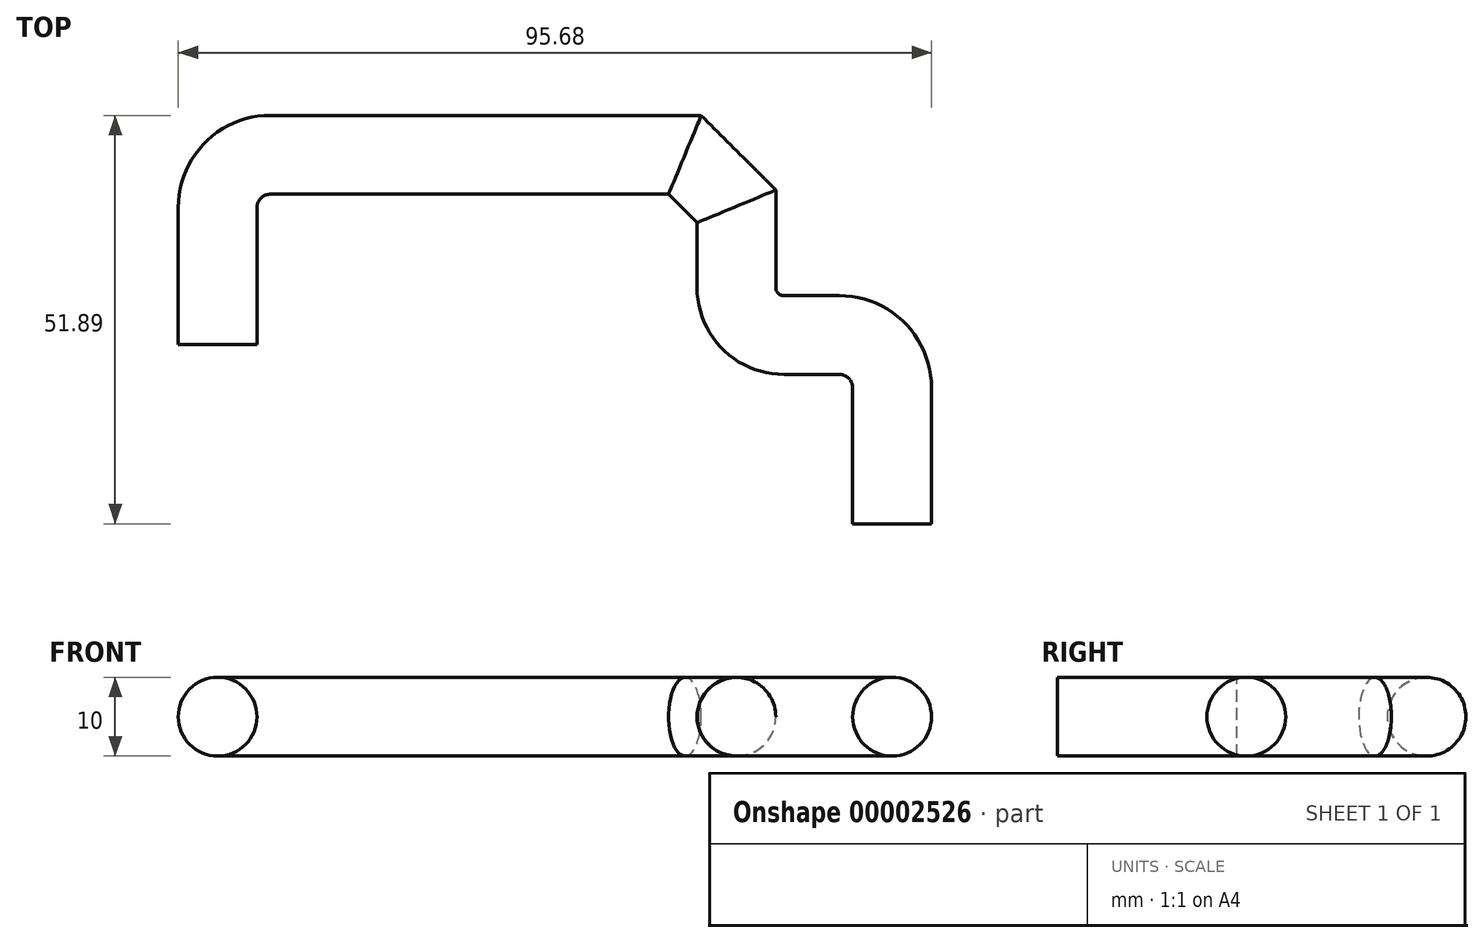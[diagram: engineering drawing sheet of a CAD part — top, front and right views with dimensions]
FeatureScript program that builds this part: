
annotation { "Feature Type Name" : "Feature", "Feature Type Description" : "" }
export const myFeature = defineFeature(function(context is Context, id is Id, definition is map)
    precondition{}
    {
        {
            var Q0;
            Q0=qCreatedBy(makeId("Top.planeOp"),FACE);
            var sketch = newSketch(context, id + "F0", { "sketchPlane" : qUnion([Q0])});
            skLineSegment(sketch, "E0", {"start": v(-28.39, -23.74) * mm, "end": v(-28.39, -6.35) * mm});
            skLineSegment(sketch, "E1", {"start": v(-22.04, 0) * mm, "end": v(30.49, 0) * mm});
            skLineSegment(sketch, "E2", {"start": v(36.84, -6.35) * mm, "end": v(36.84, -16.55) * mm});
            skLineSegment(sketch, "E3", {"start": v(43.19, -22.9) * mm, "end": v(50.26, -22.9) * mm});
            skLineSegment(sketch, "E4", {"start": v(56.6, -29.25) * mm, "end": v(56.6, -46.55) * mm});
            skPoint(sketch, "E5.visualSharp", {"position": v(-28.39, 0) * mm});
            skArc(sketch, "E5.filletArc", {"start": v(-22.04, 0) * mm, "mid": v(-26.53, -1.86) * mm, "end": v(-28.39, -6.35) * mm});
            skPoint(sketch, "E6.visualSharp", {"position": v(36.84, 0) * mm});
            skPoint(sketch, "E7.visualSharp", {"position": v(36.84, -22.9) * mm});
            skArc(sketch, "E7.filletArc", {"start": v(36.84, -16.55) * mm, "mid": v(38.7, -21.04) * mm, "end": v(43.19, -22.9) * mm});
            skPoint(sketch, "E8.visualSharp", {"position": v(56.6, -22.9) * mm});
            skArc(sketch, "E8.filletArc", {"start": v(56.6, -29.25) * mm, "mid": v(54.75, -24.76) * mm, "end": v(50.26, -22.9) * mm});
            skLineSegment(sketch, "E9", {"start": v(30.49, 0) * mm, "end": v(36.84, -6.35) * mm});
            skSolve(sketch);
        }
        {
            var Q0;
            Q0=qCreatedBy(makeId("Front.planeOp"),FACE);
            var Q1;
            Q1=sQuery(id+"F0.wireOp",VERTEX,"E0.start");
            cPlane(context, id + "F1", {"entities" : qUnion([Q0, Q1]), "cplaneType" : CPlaneType.PLANE_POINT, "offset" : 152.4 * mm, "width" : 152.4 * mm, "height" : 152.4 * mm});
        }
        {
            var Q0;
            Q0=qCreatedBy(id+"F1.planeOp",FACE);
            var sketch = newSketch(context, id + "F2", { "sketchPlane" : qUnion([Q0])});
            skCircle(sketch, "E10", {"center": v(-28.73, 0) * mm, "radius": 5 * mm});
            skSolve(sketch);
        }
        {
            var Q0;
            Q0 = qSketchRegion(id + "F2", true);
            var Q1;
            Q1=sQuery(id+"F0.wireOp",EDGE,"E0");
            var Q2;
            Q2=sQuery(id+"F0.wireOp",EDGE,"E5.filletArc");
            var Q3;
            Q3=sQuery(id+"F0.wireOp",EDGE,"E1");
            var Q4;
            Q4=sQuery(id+"F0.wireOp",EDGE,"E6.filletArc");
            var Q5;
            Q5=sQuery(id+"F0.wireOp",EDGE,"E2");
            var Q6;
            Q6=sQuery(id+"F0.wireOp",EDGE,"E7.filletArc");
            var Q7;
            Q7=sQuery(id+"F0.wireOp",EDGE,"E3");
            var Q8;
            Q8=sQuery(id+"F0.wireOp",EDGE,"E8.filletArc");
            var Q9;
            Q9=sQuery(id+"F0.wireOp",EDGE,"E4");
            var Q10;
            Q10=sQuery(id+"F0.wireOp",EDGE,"E9");
            sweep(context, id + "F3", {"profiles" : qUnion([Q0]), "path" : qUnion([Q1, Q2, Q3, Q4, Q5, Q6, Q7, Q8, Q9, Q10])});
        }
    });
